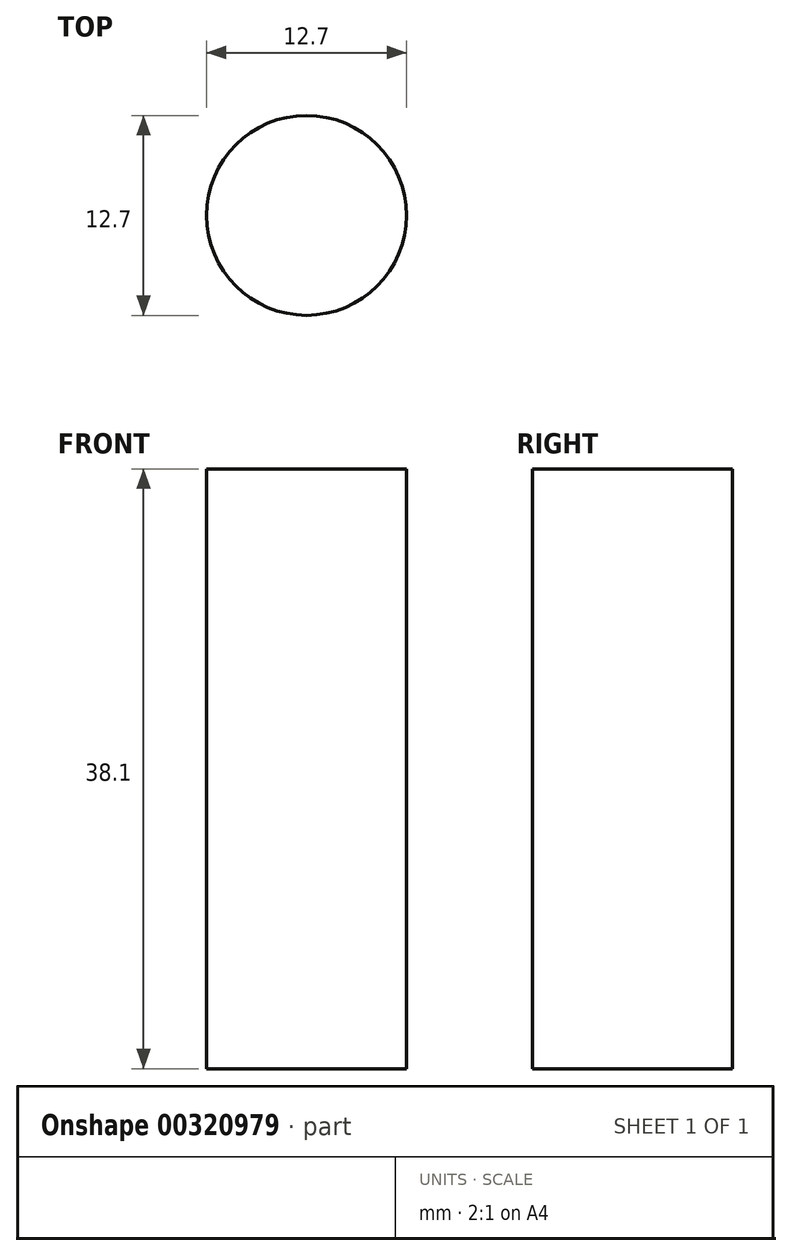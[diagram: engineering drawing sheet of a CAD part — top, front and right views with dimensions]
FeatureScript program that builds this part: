
annotation { "Feature Type Name" : "Feature", "Feature Type Description" : "" }
export const myFeature = defineFeature(function(context is Context, id is Id, definition is map)
    precondition{}
    {
        {
            var Q0;
            Q0=qCreatedBy(makeId("Top.planeOp"),FACE);
            var sketch = newSketch(context, id + "F0", { "sketchPlane" : qUnion([Q0])});
            skCircle(sketch, "E0", {"center": v(0, 0) * mm, "radius": 6.35 * mm});
            skSolve(sketch);
        }
        {
            var Q0;
            Q0=makeQuery(id+"F0.imprint","IMPRINT",FACE,{"disambiguationData":[TD([[makeQuery(id+"F0.imprint","IMPRINT",EDGE,{"derivedFrom":sQuery(id+"F0.wireOp",EDGE,"E0")}),1.0]])]});
            extrude(context, id + "F1", {"entities" : qUnion([Q0]), "endBound" : BoundingType.SYMMETRIC, "depth" : 38.1 * mm});
        }
    });
